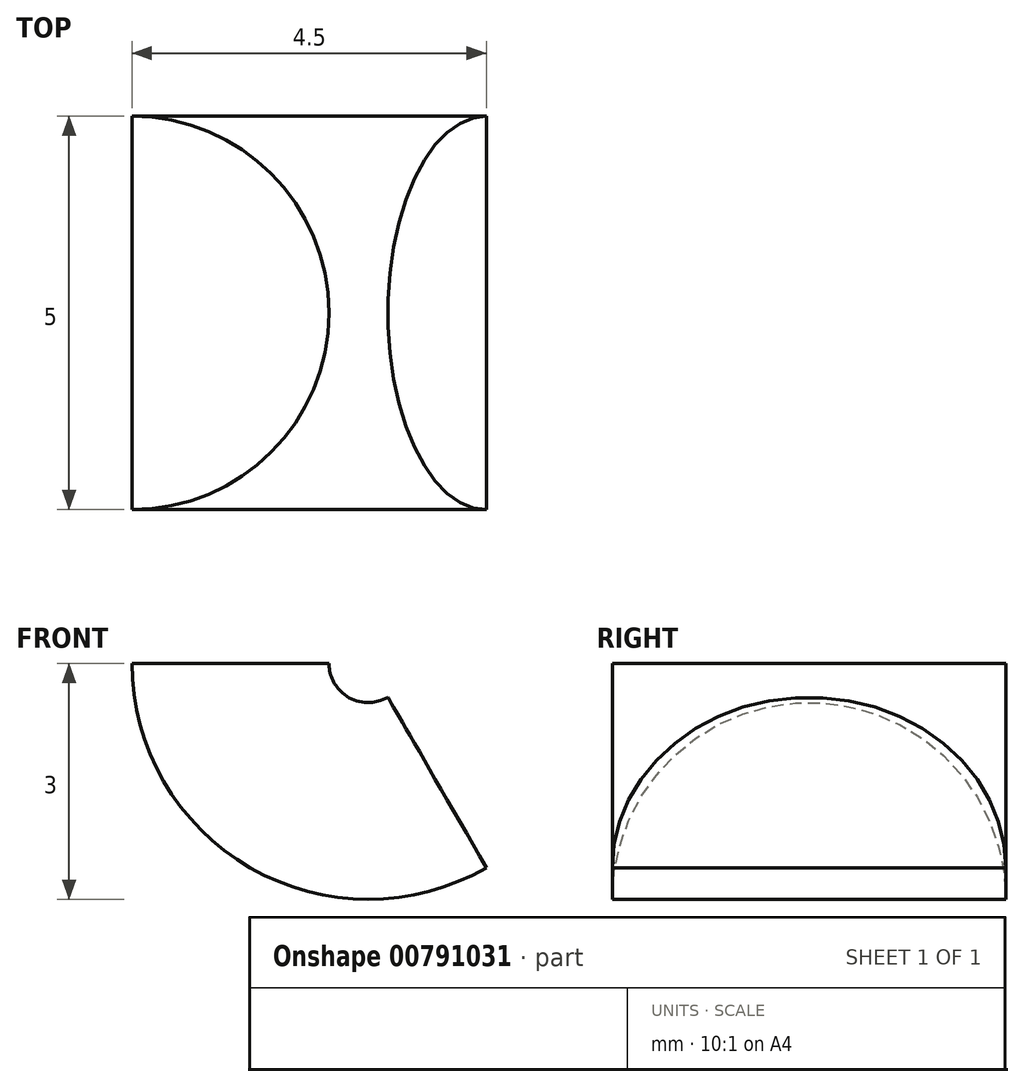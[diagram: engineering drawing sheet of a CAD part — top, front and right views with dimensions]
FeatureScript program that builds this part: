
annotation { "Feature Type Name" : "Feature", "Feature Type Description" : "" }
export const myFeature = defineFeature(function(context is Context, id is Id, definition is map)
    precondition{}
    {
        {
            var Q0;
            Q0=qCreatedBy(makeId("Top.planeOp"),FACE);
            var sketch = newSketch(context, id + "F0", { "sketchPlane" : qUnion([Q0])});
            skLineSegment(sketch, "E0", {"start": v(2.42, 0) * mm, "end": v(2.42, -5) * mm});
            skArc(sketch, "E1", {"start": v(2.42, -5) * mm, "mid": v(4.92, -2.5) * mm, "end": v(2.42, 0) * mm});
            skLineSegment(sketch, "E2", {"start": v(2.42, 0) * mm, "end": v(4.92, 0) * mm});
            skLineSegment(sketch, "E3", {"start": v(4.92, 0) * mm, "end": v(5.42, 0) * mm});
            skLineSegment(sketch, "E4", {"start": v(5.42, 0) * mm, "end": v(5.42, -15.32) * mm});
            skSolve(sketch);
        }
        {
            var Q0;
            Q0 = qSketchRegion(id + "F0", true);
            var Q1;
            Q1=sQuery(id+"F0.wireOp",EDGE,"E4");
            revolve(context, id + "F1", {"surfaceOperationType" : NewSurfaceOperationType.NEW, "entities" : qUnion([Q0]), "axis" : qUnion([Q1]), "revolveType" : RevolveType.ONE_DIRECTION, "angle" : 120 * degree});
        }
    });
